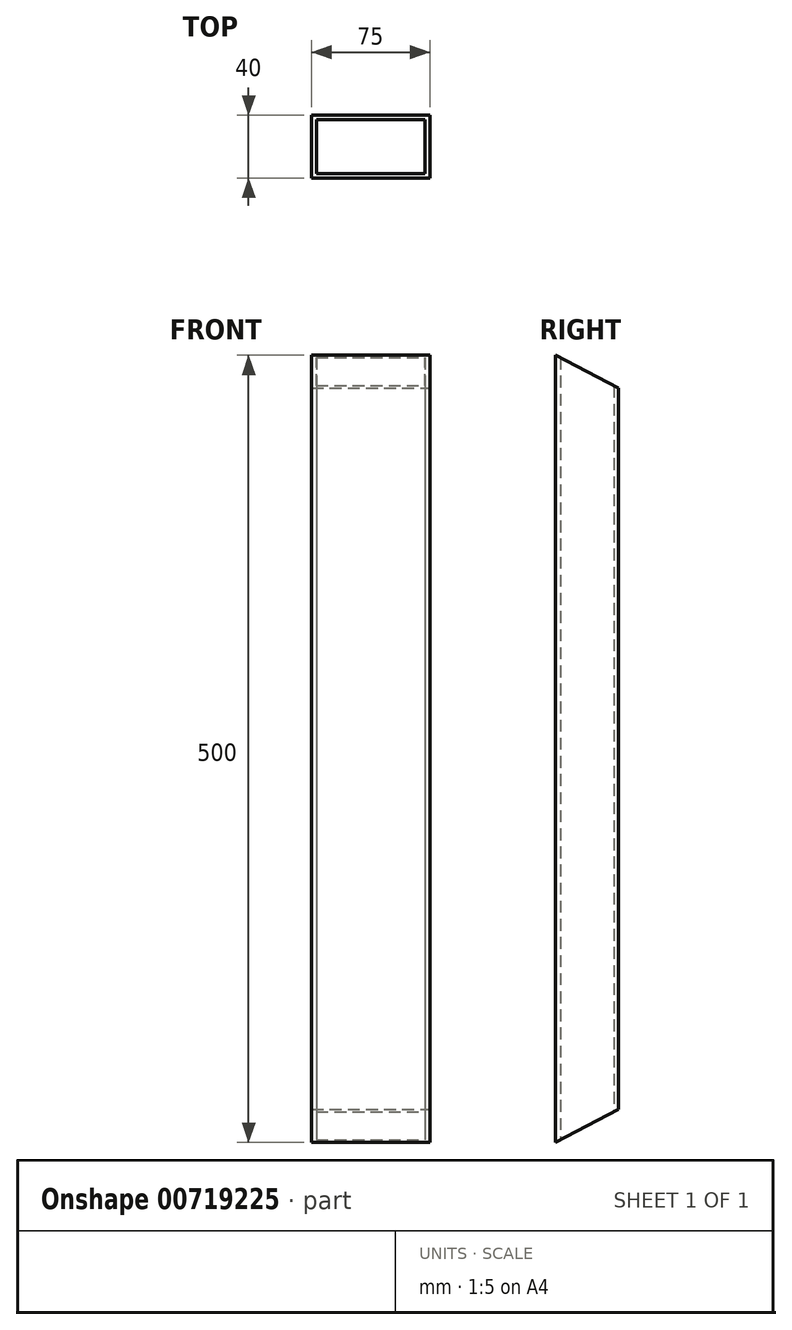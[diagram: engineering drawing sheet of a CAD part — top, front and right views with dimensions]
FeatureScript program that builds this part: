
annotation { "Feature Type Name" : "Feature", "Feature Type Description" : "" }
export const myFeature = defineFeature(function(context is Context, id is Id, definition is map)
    precondition{}
    {
        {
            var Q0;
            Q0=qCreatedBy(makeId("Top.planeOp"),FACE);
            var sketch = newSketch(context, id + "F0", { "sketchPlane" : qUnion([Q0])});
            skLineSegment(sketch, "E0.bottom", {"start": v(0, 0) * mm, "end": v(-75, 0) * mm});
            skLineSegment(sketch, "E0.top", {"start": v(0, 40) * mm, "end": v(-75, 40) * mm});
            skLineSegment(sketch, "E0.left", {"start": v(0, 0) * mm, "end": v(0, 40) * mm});
            skLineSegment(sketch, "E0.right", {"start": v(-75, 0) * mm, "end": v(-75, 40) * mm});
            skLineSegment(sketch, "E1.0", {"start": v(-3, 37) * mm, "end": v(-72, 37) * mm});
            skLineSegment(sketch, "E1.1", {"start": v(-3, 3) * mm, "end": v(-3, 37) * mm});
            skLineSegment(sketch, "E1.2", {"start": v(-3, 3) * mm, "end": v(-72, 3) * mm});
            skLineSegment(sketch, "E1.3", {"start": v(-72, 3) * mm, "end": v(-72, 37) * mm});
            skSolve(sketch);
        }
        {
            var Q0;
            Q0 = qSketchRegion(id + "F0", true);
            extrude(context, id + "F1", {"entities" : qUnion([Q0]), "depth" : 500 * mm, "offsetDistance" : 25 * mm});
        }
        {
            var Q0;
            Q0=makeQuery(id+"F1.opExtrude","SWEPT_FACE",FACE,{"disambiguationData":[OSD([sQuery(id+"F0.wireOp",EDGE,"E0.left")])]});
            var sketch = newSketch(context, id + "F2", { "sketchPlane" : qUnion([Q0])});
            skLineSegment(sketch, "E2", {"start": v(0, 0) * mm, "end": v(40, 21) * mm});
            skLineSegment(sketch, "E3", {"start": v(0, 500) * mm, "end": v(40, 479) * mm});
            skSolve(sketch);
        }
        {
            var Q0;
            {var subQ0=sQuery(id+"F2.wireOp",EDGE,"E3");Q0=makeQuery(id+"F2.imprint","IMPRINT",FACE,{"disambiguationData":[TD([[makeQuery(id+"F2.imprint","IMPRINT",EDGE,{"derivedFrom":subQ0}),1.0]])]});}
            var Q1;
            {var subQ0=sQuery(id+"F2.wireOp",EDGE,"E2");Q1=makeQuery(id+"F2.imprint","IMPRINT",FACE,{"disambiguationData":[TD([[makeQuery(id+"F2.imprint","IMPRINT",EDGE,{"derivedFrom":subQ0}),-1.0]])]});}
            var Q2;
            Q2=makeQuery(id+"F1.opExtrude","SWEPT_FACE",FACE,{"disambiguationData":[OSD([sQuery(id+"F0.wireOp",EDGE,"E0.right")])]});
            extrude(context, id + "F3", {"entities" : qUnion([Q0, Q1]), "operationType" : NewBodyOperationType.REMOVE, "endBound" : BoundingType.UP_TO_SURFACE, "oppositeDirection" : true, "depth" : 25 * mm, "endBoundEntityFace" : qUnion([Q2]), "offsetDistance" : 25 * mm});
        }
    });
